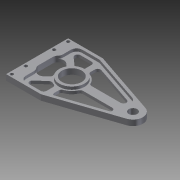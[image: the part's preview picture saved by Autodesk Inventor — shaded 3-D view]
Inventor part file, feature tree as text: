
AUTODESK INVENTOR PART (.ipt)
format: ipt  version: 2012 (Build 160160000, 160)  size: 261,120 bytes
history: native  units: in
note: dims shown in document units (in); Inventor stores cm internally (conversion verified against a paired STEP export)
features: extrude x3, fillet x3, sketch x2, hole x1
ambient origin geometry x8: Origin, YZ Plane, XZ Plane, XY Plane, X Axis, Y Axis, Z Axis, Center Point
bodies: Solid1 (feature_tree)
feature tree (9):
  sketch  "Sketch1"  dims[d0=2.75in d1=4.25in]
  extrude  "Extrusion1"  Depth=4.25in
  extrude  "Extrusion2"  Depth=0.1279in
  fillet  "Fillet1"  Radius=0.375in
  hole  "Hole1"  [1 undecoded]
  sketch  "Sketch2"  dims[d2=1.375in d6=0.1279in d7=0.375in d8=1.539in d9=0.875in d10=0.125in d11=0.0in d12=0.625in d13=0.1875in d14=0.1875in d15=0.25in d16=0.25in d17=0.125in d18=0.125in d19=0.125in d20=0.125in d21=0.125in d22=0.125in d24=0.125in d25=0.125in d26=0.25in d27=0.375in d28=0.25in d29=0.125in d30=0.0in d31=0.125in d32=0.125in d33=0.125in d35=0.125in d36=0.125in d38=0.144in d39=0.75in d40=0.25in d41=0.25in d42=0.5635in d43=1.0in d44=0.8108in d45=0.5in d46=0.125in d47=0.125in d48=0.125in d49=0.125in d51=0.125in d53=0.875in d54=0.0625in d58=0.125in d59=0.0in d62=0.75in d63=0.75in d69=0.125in d70=0.1279in d71=0.4375in d72=1.125in d73=0.25in d74=0.25in]
  extrude  "Extrusion4"  Depth=0.875in
  fillet  "Fillet6"  Radius=0.125in
  fillet  "Fillet7"  Radius=0.625in
note: 1 required parameter value undecoded (feature->parameter linkage not recoverable at this tier; creation-order binding heuristic only, values carry confidence <= 0.55)
